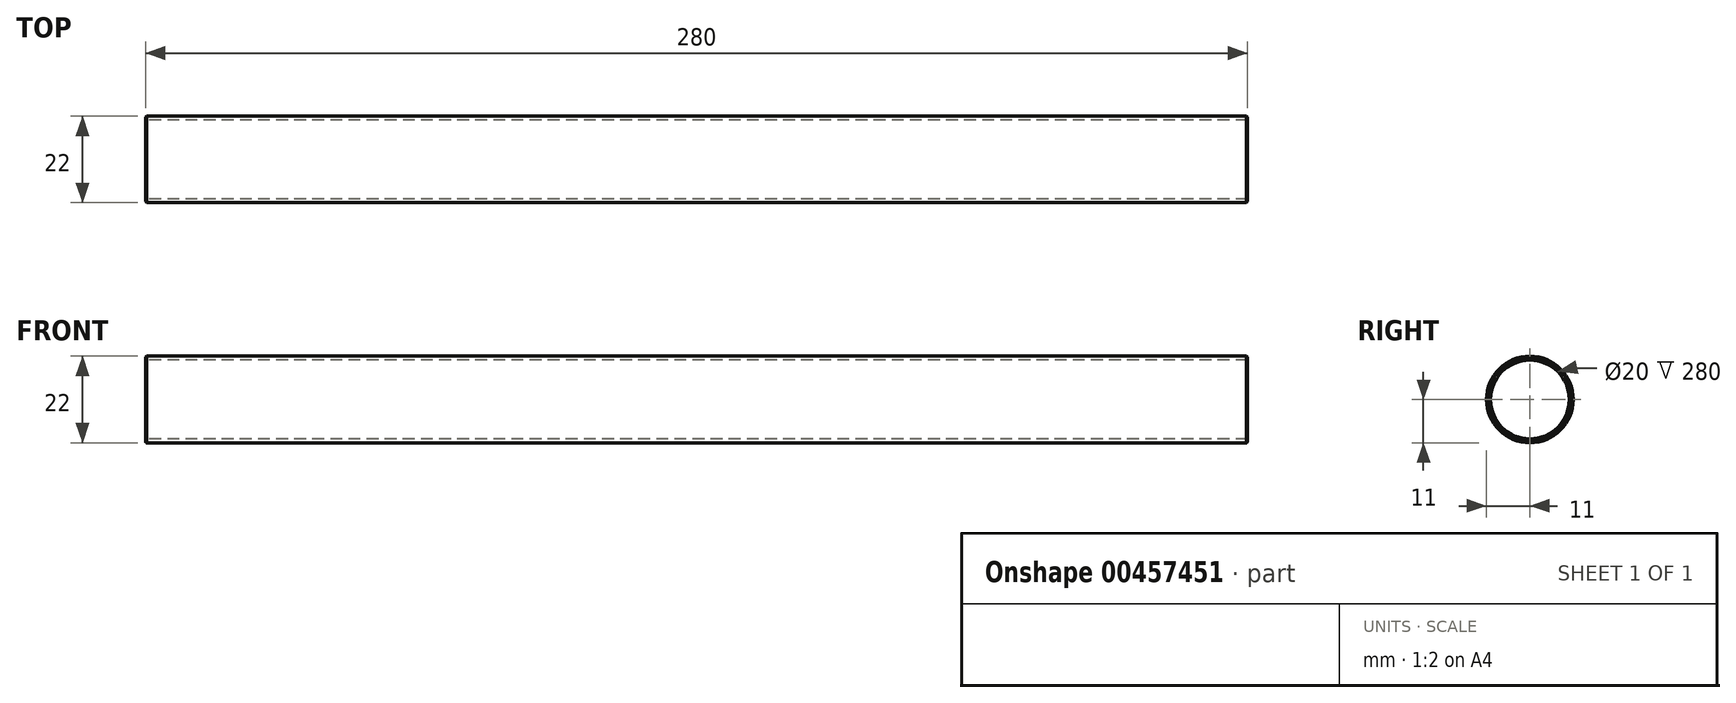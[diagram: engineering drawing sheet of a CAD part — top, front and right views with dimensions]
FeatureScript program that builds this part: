
annotation { "Feature Type Name" : "Feature", "Feature Type Description" : "" }
export const myFeature = defineFeature(function(context is Context, id is Id, definition is map)
    precondition{}
    {
        {
            var Q0;
            Q0=qCreatedBy(makeId("Right.planeOp"),FACE);
            var sketch = newSketch(context, id + "F0", { "sketchPlane" : qUnion([Q0])});
            skCircle(sketch, "E0", {"center": v(0, 0) * mm, "radius": 11 * mm});
            skCircle(sketch, "E1", {"center": v(0, 0) * mm, "radius": 10 * mm});
            skSolve(sketch);
        }
        {
            var Q0;
            Q0=makeQuery(id+"F0.imprint","IMPRINT",FACE,{"disambiguationData":[TD([[makeQuery(id+"F0.imprint","IMPRINT",EDGE,{"derivedFrom":sQuery(id+"F0.wireOp",EDGE,"E0")}),1.0]])]});
            extrude(context, id + "F1", {"entities" : qUnion([Q0]), "depth" : 280 * mm, "symmetric" : true});
        }
        {
            var Q0;
            Q0=makeQuery(id+"F1.opExtrude","CAP_EDGE",EDGE,{"disambiguationData":[OSD([sQuery(id+"F0.wireOp",EDGE,"E0")])],"isStart":true});
            var Q1;
            Q1=makeQuery(id+"F1.opExtrude","CAP_EDGE",EDGE,{"disambiguationData":[OSD([sQuery(id+"F0.wireOp",EDGE,"E0")])],"isStart":false});
            chamfer(context, id + "F2", {"entities" : qUnion([Q0, Q1]), "width" : 0.25 * mm, "tangentPropagation" : true});
        }
        {
            var Q0;
            Q0=makeQuery(id+"F1.opExtrude","CAP_FACE",FACE,{"disambiguationData":[OSD([sQuery(id+"F0.wireOp",EDGE,"E0"),sQuery(id+"F0.wireOp",EDGE,"E1")])],"isStart":false});
            cPlane(context, id + "F3", {"entities" : qUnion([Q0]), "cplaneType" : CPlaneType.OFFSET, "offset" : 25 * mm, "oppositeDirection" : true, "width" : 150 * mm, "height" : 150 * mm});
        }
        {
            var Q0;
            Q0=qCreatedBy(id+"F3.planeOp",FACE);
            var sketch = newSketch(context, id + "F4", { "sketchPlane" : qUnion([Q0])});
            skCircle(sketch, "E2.0", {"center": v(0, 0) * mm, "radius": 10 * mm});
            skSolve(sketch);
        }
    });
